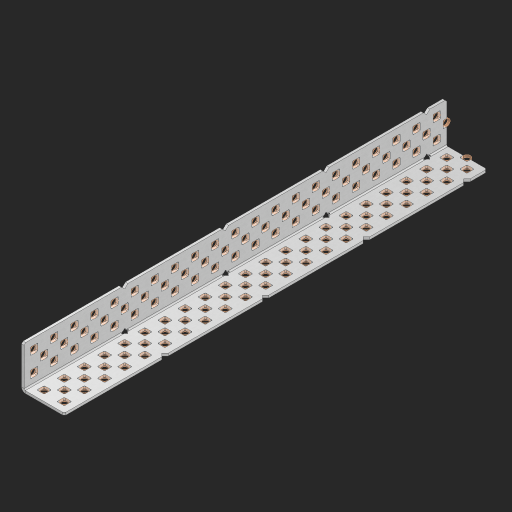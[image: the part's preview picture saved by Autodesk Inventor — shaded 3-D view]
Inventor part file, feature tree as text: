
AUTODESK INVENTOR PART (.ipt)
format: ipt  version: 2023 (Build 270158000, 158)  size: 1,606,144 bytes
history: native  units: in
note: dims shown in document units (in); Inventor stores cm internally (conversion verified against a paired STEP export)
features: other x132, extrude x124, sheet_metal_op x8, sketch x7, pattern_linear x2, mirror x1, chamfer x1
ambient origin geometry x8: Origin, YZ Plane, XZ Plane, XY Plane, X Axis, Y Axis, Z Axis, Center Point
bodies: Solid1 (feature_tree), Body (feature_tree)
feature tree (275):
  sheet_metal_op  "Flanges"
  sheet_metal_op  "Body Pattern"
  pattern_linear  "Center Pattern"  Spacing1=1.0in  [1 undecoded]
  other  "Arc Length"
  pattern_linear  "Notch Pattern"  Spacing1=0.25in  [1 undecoded]
  other  "Diagonal Plane"
  mirror  "Everything Mirrored"
  chamfer  "End Chamfer"
  sketch  "Sketch1"  dims[d0=1.0in]
  other  "Plate1"
  sketch  "Sketch2"  dims[d1=10.5in]
  other  "Plate2"
  sheet_metal_op  "Bend1"
  sheet_metal_op  "Corner1"
  sketch  "Sketch8"  dims[d2=0.0625in]
  sketch  "Sketch9"  dims[d3=0.0625in]
  other  "Srf91"
  sheet_metal_op  "Body Pattern Sketch"
  other  "Srf92"
  sketch  "Sketch13"  dims[d4=0.0312in]
  sketch  "Sketch15"  dims[d5=0.125in]
  sketch  "Sketch16"  dims[d6=0.0625in d7=1.0in d8=90.0deg d9=0.0312in d10=0.25in d11=0.0625in d12=0.0625in d49=0.182in d50=0.02in d52=0.25in d53=0.0625in d54=0.0in d55=0.172in d56=1.0in d57=0.0in d60=8.2677in d62=0.5in d63=0.7874in d65=0.5in d85=0.1473in d86=0.1782in d89=0.0625in d90=0.0in d91=0.04in d92=0.0491in d95=2.5in d96=0.04in d97=0.25in d98=45.0deg d99=0.25in d106=0.182in d107=0.02in d108=0.5in d110=0.0625in d111=0.0in d112=0.172in d113=0.5in d114=0.0in d117=0.5in d123=0.25in d125=0.25in d126=0.0491in d127=0.1473in d128=0.08in d129=0.04in d130=2.5in]
  other  "Srf786"
  other  "Srf856"
  other  "Srf857"
  other  "Srf858"
  other  "Srf859"
  other  "Srf860"
  other  "Srf861"
  other  "Srf889"
  other  "Srf890"
  other  "Srf891"
  other  "Srf1275"
  other  "Srf1276"
  other  "Srf1278"
  other  "Srf1279"
  other  "Srf1280"
  other  "Srf1281"
  other  "Srf1282"
  other  "Srf1283"
  other  "Srf1277"
  other  "Srf1285"
  other  "Srf1286"
  other  "Srf1287"
  other  "Srf1383"
  other  "Srf1384"
  other  "Srf1385"
  other  "Srf1386"
  other  "Srf1387"
  other  "Srf1388"
  other  "Srf1389"
  other  "Srf1390"
  other  "Srf1391"
  other  "Srf1392"
  other  "Srf1393"
  other  "Srf1394"
  other  "Srf1395"
  other  "Srf1396"
  other  "Srf1397"
  other  "Srf1398"
  other  "Srf1399"
  other  "Srf1400"
  other  "Srf1401"
  other  "Srf1402"
  other  "Srf1403"
  other  "Srf1404"
  other  "Srf1405"
  other  "Srf1406"
  other  "Srf1407"
  other  "Srf1408"
  other  "Srf1409"
  other  "Srf1410"
  other  "Srf1411"
  other  "Srf1412"
  other  "Srf1413"
  other  "Srf1414"
  other  "Srf1415"
  other  "Srf1416"
  other  "Srf1445"
  other  "Srf1446"
  other  "Srf1447"
  other  "Srf1448"
  other  "Srf1449"
  other  "Srf1450"
  other  "Srf1451"
  other  "Srf1452"
  other  "Srf1453"
  other  "Srf1454"
  other  "Srf1455"
  other  "Srf1456"
  other  "Srf1457"
  other  "Srf1458"
  other  "Srf1459"
  other  "Srf1460"
  other  "Srf1461"
  other  "Srf1475"
  other  "Srf1476"
  other  "Srf1477"
  other  "Srf1478"
  other  "Srf1479"
  other  "Srf1480"
  other  "Srf1481"
  other  "Srf1482"
  other  "Srf1483"
  other  "Srf1484"
  other  "Srf1485"
  other  "Srf1486"
  other  "Srf1487"
  other  "Srf1488"
  other  "Srf1489"
  other  "Srf1490"
  other  "Srf1491"
  other  "Srf1492"
  other  "Srf1493"
  other  "Srf1494"
  other  "Srf1495"
  other  "Srf1496"
  other  "Srf1497"
  other  "Srf1498"
  other  "Srf1499"
  other  "Srf1500"
  other  "Srf1501"
  other  "Srf1502"
  other  "Srf1503"
  other  "Srf1504"
  other  "Srf1505"
  other  "Srf1506"
  other  "Srf1507"
  other  "Srf1508"
  other  "Srf1537"
  other  "Srf1538"
  other  "Srf1539"
  other  "Srf1540"
  other  "Srf1541"
  other  "Srf1542"
  other  "Srf1543"
  other  "Srf1544"
  other  "Srf1545"
  other  "Srf1546"
  other  "Srf1547"
  other  "Srf1548"
  other  "Srf1549"
  other  "Srf1550"
  other  "Srf1551"
  other  "Srf1552"
  other  "Srf1553"
  sheet_metal_op  "Body Stamp"
  sheet_metal_op  "Body Circle"
  other  "Center Stamp"
  other  "Center Circle"
  sheet_metal_op  "Notch"
  extrude  "ExtrusionSrf92"  Depth=0.0625in
  extrude  "ExtrusionSrf856"  Depth=0.0625in
  extrude  "ExtrusionSrf857"  Depth=0.182in
  extrude  "ExtrusionSrf858"  Depth=0.02in
  extrude  "ExtrusionSrf859"  Depth=0.25in
  extrude  "ExtrusionSrf860"  Depth=0.0625in
  extrude  "ExtrusionSrf861"  TaperAngle=0.0deg  [1 undecoded]
  extrude  "ExtrusionSrf889"  Depth=2.5in
  extrude  "ExtrusionSrf890"  Depth=1.0in TaperAngle=0.0deg
  extrude  "ExtrusionSrf891"  Depth=2.5in
  extrude  "ExtrusionSrf1275"  Depth=0.5in
  extrude  "ExtrusionSrf1276"  Depth=2.5in
  extrude  "ExtrusionSrf1277"  Depth=2.5in
  extrude  "ExtrusionSrf1278"  Depth=0.0625in
  extrude  "ExtrusionSrf1279"  Depth=2.5in TaperAngle=0.0deg
  extrude  "ExtrusionSrf1280"  Depth=2.5in
  extrude  "ExtrusionSrf1281"  Depth=0.25in TaperAngle=45.0deg
  extrude  "ExtrusionSrf1282"  Depth=0.25in
  extrude  "ExtrusionSrf1345"  Depth=0.182in
  extrude  "ExtrusionSrf1346"  Depth=0.02in
  extrude  "ExtrusionSrf1347"  Depth=0.5in
  extrude  "ExtrusionSrf1348"  Depth=0.0625in
  extrude  "ExtrusionSrf1383"  TaperAngle=0.0deg  [1 undecoded]
  extrude  "ExtrusionSrf1384"  Depth=2.5in
  extrude  "ExtrusionSrf1385"  Depth=0.5in TaperAngle=0.0deg
  extrude  "ExtrusionSrf1386"  Depth=0.5in
  extrude  "ExtrusionSrf1387"  Depth=0.25in
  extrude  "ExtrusionSrf1388"  Depth=0.25in
  extrude  "ExtrusionSrf1389"  Depth=2.5in
  extrude  "ExtrusionSrf1390"  Depth=2.5in
  extrude  "ExtrusionSrf1391"  Depth=2.5in
  extrude  "ExtrusionSrf1392"  Depth=2.5in
  extrude  "ExtrusionSrf1393"  Depth=2.5in
  extrude  "ExtrusionSrf1394"  [1 undecoded]
  extrude  "ExtrusionSrf1395"  [1 undecoded]
  extrude  "ExtrusionSrf1396"  [1 undecoded]
  extrude  "ExtrusionSrf1397"  [1 undecoded]
  extrude  "ExtrusionSrf1398"  [1 undecoded]
  extrude  "ExtrusionSrf1399"  [1 undecoded]
  extrude  "ExtrusionSrf1400"  [1 undecoded]
  extrude  "ExtrusionSrf1401"  [1 undecoded]
  extrude  "ExtrusionSrf1402"  [1 undecoded]
  extrude  "ExtrusionSrf1403"  [1 undecoded]
  extrude  "ExtrusionSrf1404"  [1 undecoded]
  extrude  "ExtrusionSrf1405"  [1 undecoded]
  extrude  "ExtrusionSrf1406"  [1 undecoded]
  extrude  "ExtrusionSrf1407"  [1 undecoded]
  extrude  "ExtrusionSrf1408"  [1 undecoded]
  extrude  "ExtrusionSrf1409"  [1 undecoded]
  extrude  "ExtrusionSrf1410"  [1 undecoded]
  extrude  "ExtrusionSrf1411"  [1 undecoded]
  extrude  "ExtrusionSrf1412"  [1 undecoded]
  extrude  "ExtrusionSrf1413"  [1 undecoded]
  extrude  "ExtrusionSrf1414"  [1 undecoded]
  extrude  "ExtrusionSrf1415"  [1 undecoded]
  extrude  "ExtrusionSrf1416"  [1 undecoded]
  extrude  "ExtrusionSrf1445"  [1 undecoded]
  extrude  "ExtrusionSrf1446"  [1 undecoded]
  extrude  "ExtrusionSrf1447"  [1 undecoded]
  extrude  "ExtrusionSrf1448"  [1 undecoded]
  extrude  "ExtrusionSrf1449"  [1 undecoded]
  extrude  "ExtrusionSrf1450"  [1 undecoded]
  extrude  "ExtrusionSrf1451"  [1 undecoded]
  extrude  "ExtrusionSrf1452"  [1 undecoded]
  extrude  "ExtrusionSrf1453"  [1 undecoded]
  extrude  "ExtrusionSrf1454"  [1 undecoded]
  extrude  "ExtrusionSrf1455"  [1 undecoded]
  extrude  "ExtrusionSrf1456"  [1 undecoded]
  extrude  "ExtrusionSrf1457"  [1 undecoded]
  extrude  "ExtrusionSrf1458"  [1 undecoded]
  extrude  "ExtrusionSrf1459"  [1 undecoded]
  extrude  "ExtrusionSrf1460"  [1 undecoded]
  extrude  "ExtrusionSrf1461"  [1 undecoded]
  extrude  "ExtrusionSrf1475"  [1 undecoded]
  extrude  "ExtrusionSrf1476"  [1 undecoded]
  extrude  "ExtrusionSrf1477"  [1 undecoded]
  extrude  "ExtrusionSrf1478"  [1 undecoded]
  extrude  "ExtrusionSrf1479"  [1 undecoded]
  extrude  "ExtrusionSrf1480"  [1 undecoded]
  extrude  "ExtrusionSrf1481"  [1 undecoded]
  extrude  "ExtrusionSrf1482"  [1 undecoded]
  extrude  "ExtrusionSrf1483"  [1 undecoded]
  extrude  "ExtrusionSrf1484"  [1 undecoded]
  extrude  "ExtrusionSrf1485"  [1 undecoded]
  extrude  "ExtrusionSrf1486"  [1 undecoded]
  extrude  "ExtrusionSrf1487"  [1 undecoded]
  extrude  "ExtrusionSrf1488"  [1 undecoded]
  extrude  "ExtrusionSrf1489"  [1 undecoded]
  extrude  "ExtrusionSrf1490"  [1 undecoded]
  extrude  "ExtrusionSrf1491"  [1 undecoded]
  extrude  "ExtrusionSrf1492"  [1 undecoded]
  extrude  "ExtrusionSrf1493"  [1 undecoded]
  extrude  "ExtrusionSrf1494"  [1 undecoded]
  extrude  "ExtrusionSrf1495"  [1 undecoded]
  extrude  "ExtrusionSrf1496"  [1 undecoded]
  extrude  "ExtrusionSrf1497"  [1 undecoded]
  extrude  "ExtrusionSrf1498"  [1 undecoded]
  extrude  "ExtrusionSrf1499"  [1 undecoded]
  extrude  "ExtrusionSrf1500"  [1 undecoded]
  extrude  "ExtrusionSrf1501"  [1 undecoded]
  extrude  "ExtrusionSrf1502"  [1 undecoded]
  extrude  "ExtrusionSrf1503"  [1 undecoded]
  extrude  "ExtrusionSrf1504"  [1 undecoded]
  extrude  "ExtrusionSrf1505"  [1 undecoded]
  extrude  "ExtrusionSrf1506"  [1 undecoded]
  extrude  "ExtrusionSrf1507"  [1 undecoded]
  extrude  "ExtrusionSrf1508"  [1 undecoded]
  extrude  "ExtrusionSrf1537"  [1 undecoded]
  extrude  "ExtrusionSrf1538"  [1 undecoded]
  extrude  "ExtrusionSrf1539"  [1 undecoded]
  extrude  "ExtrusionSrf1540"  [1 undecoded]
  extrude  "ExtrusionSrf1541"  [1 undecoded]
  extrude  "ExtrusionSrf1542"  [1 undecoded]
  extrude  "ExtrusionSrf1543"  [1 undecoded]
  extrude  "ExtrusionSrf1544"  [1 undecoded]
  extrude  "ExtrusionSrf1545"  [1 undecoded]
  extrude  "ExtrusionSrf1546"  [1 undecoded]
  extrude  "ExtrusionSrf1547"  [1 undecoded]
  extrude  "ExtrusionSrf1548"  [1 undecoded]
  extrude  "ExtrusionSrf1549"  [1 undecoded]
  extrude  "ExtrusionSrf1550"  [1 undecoded]
  extrude  "ExtrusionSrf1551"  [1 undecoded]
  extrude  "ExtrusionSrf1552"  [1 undecoded]
  extrude  "ExtrusionSrf1553"  [1 undecoded]
note: 95 required parameter values undecoded (feature->parameter linkage not recoverable at this tier; creation-order binding heuristic only, values carry confidence <= 0.55)
